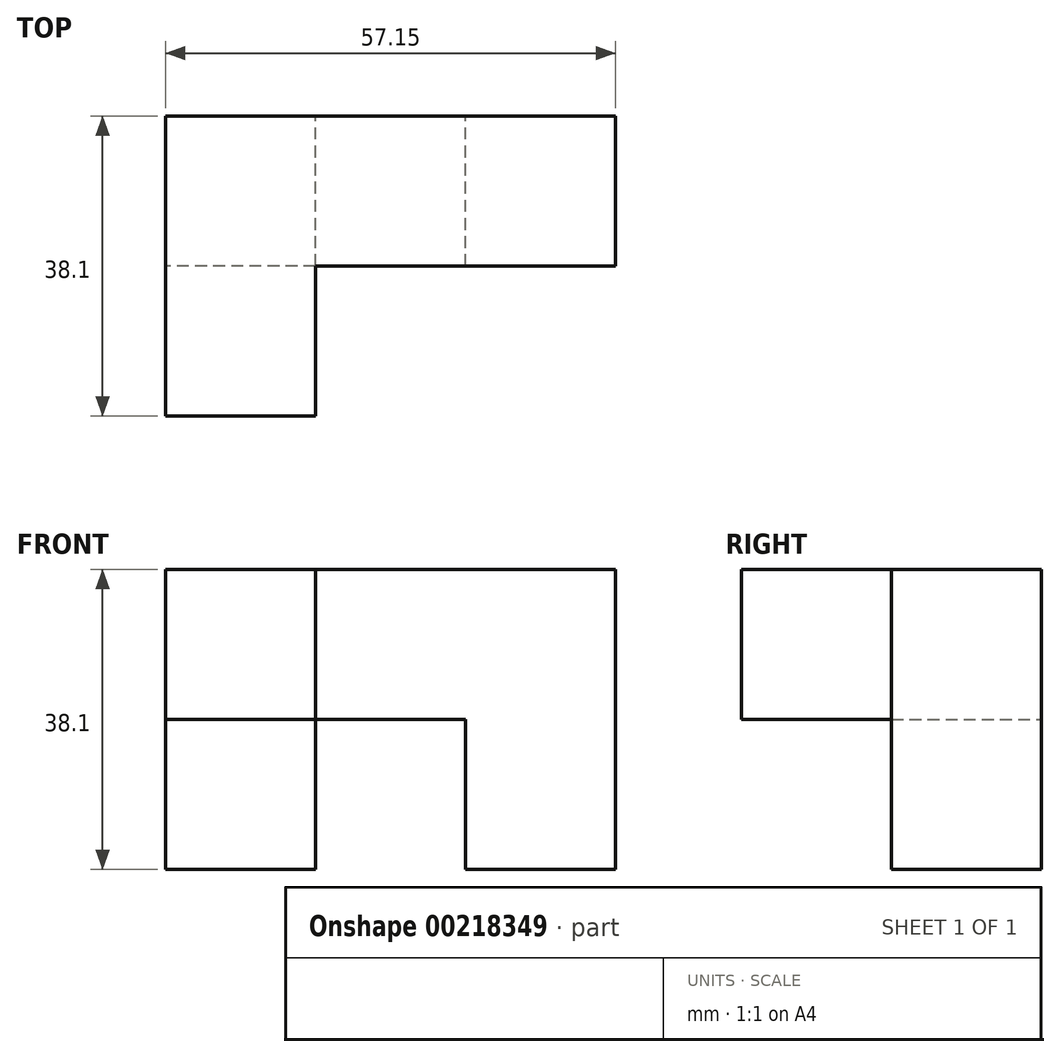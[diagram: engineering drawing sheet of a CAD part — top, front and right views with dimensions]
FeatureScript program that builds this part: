
annotation { "Feature Type Name" : "Feature", "Feature Type Description" : "" }
export const myFeature = defineFeature(function(context is Context, id is Id, definition is map)
    precondition{}
    {
        {
            var Q0;
            Q0=qCreatedBy(makeId("Front.planeOp"),FACE);
            var sketch = newSketch(context, id + "F0", { "sketchPlane" : qUnion([Q0])});
            skLineSegment(sketch, "E0.bottom", {"start": v(0, 0) * mm, "end": v(-19.05, 0) * mm});
            skLineSegment(sketch, "E0.top", {"start": v(0, 19.05) * mm, "end": v(-19.05, 19.05) * mm});
            skLineSegment(sketch, "E0.left", {"start": v(0, 0) * mm, "end": v(0, 19.05) * mm});
            skLineSegment(sketch, "E0.right", {"start": v(-19.05, 0) * mm, "end": v(-19.05, 19.05) * mm});
            skLineSegment(sketch, "E1.top", {"start": v(0, -19.05) * mm, "end": v(-19.05, -19.05) * mm});
            skLineSegment(sketch, "E1.left", {"start": v(0, 0) * mm, "end": v(0, -19.05) * mm});
            skLineSegment(sketch, "E1.right", {"start": v(-19.05, 0) * mm, "end": v(-19.05, -19.05) * mm});
            skLineSegment(sketch, "E2.bottom", {"start": v(0, 19.05) * mm, "end": v(19.05, 19.05) * mm});
            skLineSegment(sketch, "E2.top", {"start": v(0, 0) * mm, "end": v(19.05, 0) * mm});
            skLineSegment(sketch, "E2.left", {"start": v(0, 19.05) * mm, "end": v(0, 0) * mm});
            skLineSegment(sketch, "E2.right", {"start": v(19.05, 19.05) * mm, "end": v(19.05, 0) * mm});
            skLineSegment(sketch, "E3.bottom", {"start": v(19.05, 0) * mm, "end": v(38.1, 0) * mm});
            skLineSegment(sketch, "E3.top", {"start": v(19.05, 19.05) * mm, "end": v(38.1, 19.05) * mm});
            skLineSegment(sketch, "E3.left", {"start": v(19.05, 0) * mm, "end": v(19.05, 19.05) * mm});
            skLineSegment(sketch, "E3.right", {"start": v(38.1, 0) * mm, "end": v(38.1, 19.05) * mm});
            skLineSegment(sketch, "E4.bottom", {"start": v(38.1, 0) * mm, "end": v(19.05, 0) * mm});
            skLineSegment(sketch, "E4.top", {"start": v(38.1, -19.05) * mm, "end": v(19.05, -19.05) * mm});
            skLineSegment(sketch, "E4.left", {"start": v(38.1, 0) * mm, "end": v(38.1, -19.05) * mm});
            skLineSegment(sketch, "E4.right", {"start": v(19.05, 0) * mm, "end": v(19.05, -19.05) * mm});
            skSolve(sketch);
        }
        {
            var Q0;
            Q0=makeQuery(id+"F0.imprint","IMPRINT",FACE,{"disambiguationData":[TD([[makeQuery(id+"F0.imprint","IMPRINT",EDGE,{"derivedFrom":sQuery(id+"F0.wireOp",EDGE,"E0.top")}),1.0]])]});
            extrude(context, id + "F1", {"entities" : qUnion([Q0]), "depth" : 38.1 * mm});
        }
        {
            var Q0;
            Q0 = qSketchRegion(id + "F0", true);
            extrude(context, id + "F2", {"entities" : qUnion([Q0]), "operationType" : NewBodyOperationType.ADD, "depth" : 19.05 * mm});
        }
    });
